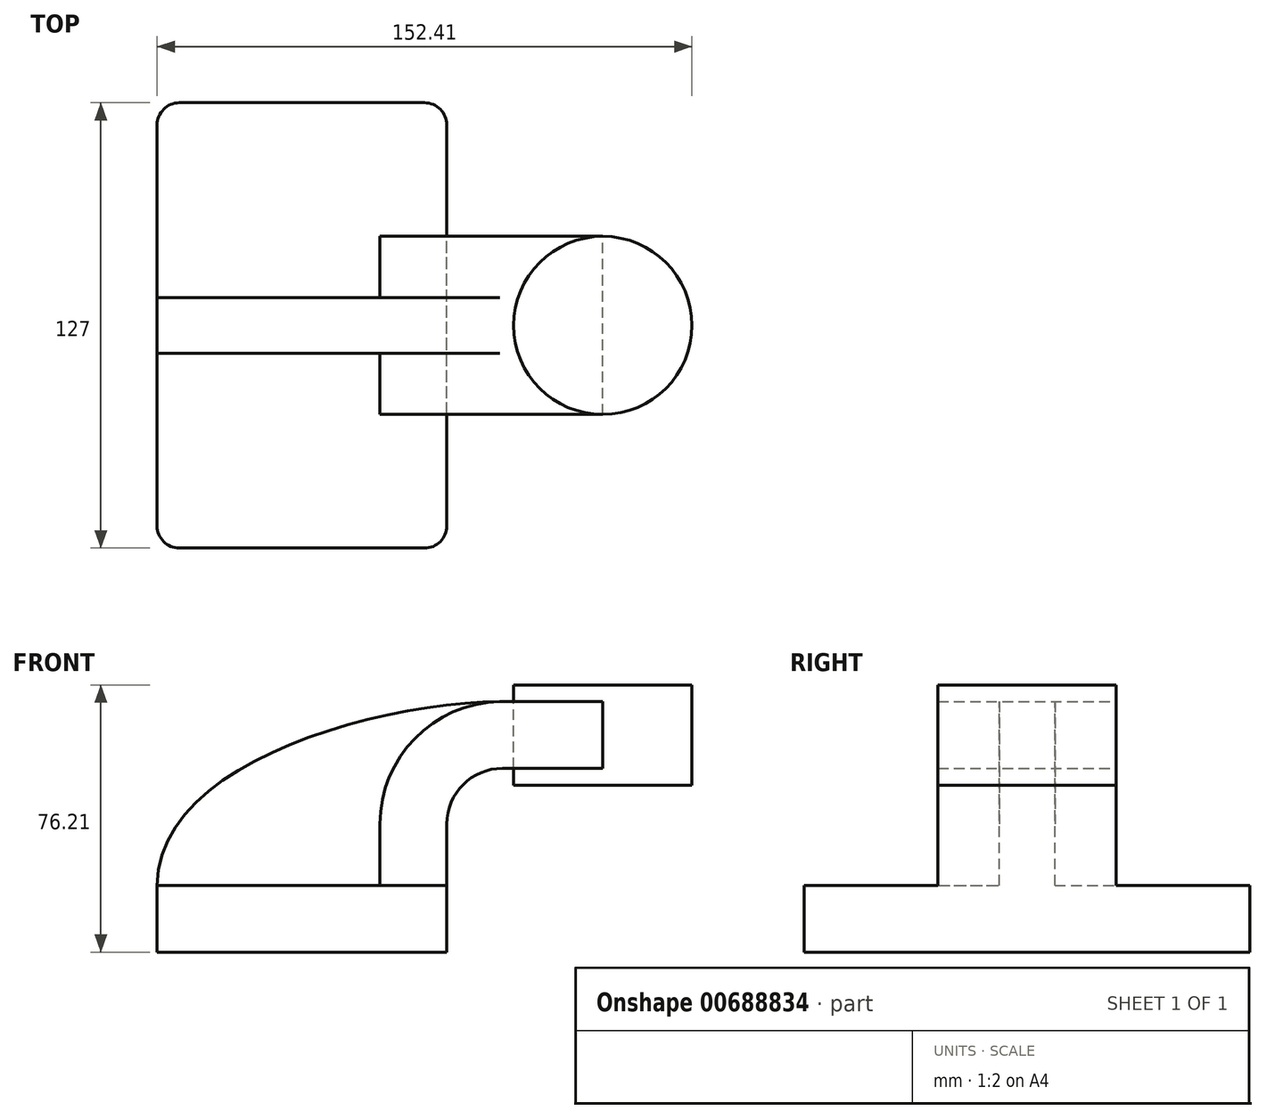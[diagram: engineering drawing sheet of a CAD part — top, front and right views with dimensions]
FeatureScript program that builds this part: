
annotation { "Feature Type Name" : "Feature", "Feature Type Description" : "" }
export const myFeature = defineFeature(function(context is Context, id is Id, definition is map)
    precondition{}
    {
        {
            var Q0;
            Q0=qCreatedBy(makeId("Front.planeOp"),FACE);
            var sketch = newSketch(context, id + "F0", { "sketchPlane" : qUnion([Q0])});
            skLineSegment(sketch, "E0.bottom", {"start": v(-41.28, 9.52) * mm, "end": v(41.27, 9.53) * mm});
            skLineSegment(sketch, "E0.top", {"start": v(-41.28, -9.53) * mm, "end": v(41.28, -9.53) * mm});
            skLineSegment(sketch, "E0.left", {"start": v(-41.28, 9.52) * mm, "end": v(-41.27, -9.53) * mm});
            skLineSegment(sketch, "E0.right", {"start": v(41.28, 9.53) * mm, "end": v(41.28, -9.52) * mm});
            skPoint(sketch, "E0.middle", {"position": v(0, 0) * mm});
            skLineSegment(sketch, "E1.bottom", {"start": v(60.32, 38.1) * mm, "end": v(111.12, 38.1) * mm});
            skLineSegment(sketch, "E1.top", {"start": v(60.32, 66.68) * mm, "end": v(111.12, 66.68) * mm});
            skLineSegment(sketch, "E1.left", {"start": v(60.32, 38.1) * mm, "end": v(60.32, 66.68) * mm});
            skLineSegment(sketch, "E1.right", {"start": v(111.12, 38.1) * mm, "end": v(111.12, 66.68) * mm});
            skPoint(sketch, "E1.middle", {"position": v(85.72, 52.39) * mm});
            skLineSegment(sketch, "E2", {"start": v(41.27, 9.53) * mm, "end": v(41.27, 27) * mm});
            skArc(sketch, "E3", {"start": v(41.27, 27) * mm, "mid": v(45.92, 38.23) * mm, "end": v(57.15, 42.88) * mm});
            skLineSegment(sketch, "E4", {"start": v(57.15, 42.88) * mm, "end": v(85.72, 42.88) * mm});
            skLineSegment(sketch, "E5.0", {"start": v(57.15, 61.93) * mm, "end": v(85.72, 61.93) * mm});
            skArc(sketch, "E5.1", {"start": v(22.22, 27) * mm, "mid": v(32.45, 51.7) * mm, "end": v(57.15, 61.93) * mm});
            skLineSegment(sketch, "E5.2", {"start": v(22.22, 9.53) * mm, "end": v(22.22, 27) * mm});
            skFitSpline(sketch, "E6", {"points": [v(-41.28, 9.53) * mm, v(57.15, 61.93) * mm], "startDerivative": vector(0.27, 104.66) * mm, "endDerivative": vector(108.7, 0.8) * mm});
            skLineSegment(sketch, "E7", {"start": v(85.72, 61.93) * mm, "end": v(85.72, 42.88) * mm});
            skLineSegment(sketch, "E8", {"start": v(60.32, 61.93) * mm, "end": v(60.32, 42.88) * mm});
            skLineSegment(sketch, "E9", {"start": v(85.72, 66.67) * mm, "end": v(85.72, 38.1) * mm});
            skSolve(sketch);
        }
        {
            var Q0;
            Q0=makeQuery(id+"F0.imprint","IMPRINT",FACE,{"disambiguationData":[TD([[makeQuery(id+"F0.imprint","IMPRINT",EDGE,{"derivedFrom":sQuery(id+"F0.wireOp",EDGE,"E0.top")}),1.0]])]});
            extrude(context, id + "F1", {"entities" : qUnion([Q0]), "endBound" : BoundingType.SYMMETRIC, "depth" : 127 * mm, "offsetDistance" : 25.4 * mm});
        }
        {
            var Q0;
            {var subQ0=sQuery(id+"F0.wireOp",EDGE,"E7");Q0=makeQuery(id+"F0.imprint","IMPRINT",FACE,{"disambiguationData":[TD([[makeQuery(id+"F0.imprint","IMPRINT",EDGE,{"derivedFrom":subQ0}),-1.0]])]});}
            var Q1;
            {var subQ4=sQuery(id+"F0.wireOp",EDGE,"E2");Q1=makeQuery(id+"F0.imprint","IMPRINT",FACE,{"disambiguationData":[TD([[makeQuery(id+"F0.imprint","IMPRINT",EDGE,{"derivedFrom":subQ4}),1.0]])]});}
            var Q2;
            {var subQ3=sQuery(id+"F0.wireOp",EDGE,"E8");Q2=makeQuery(id+"F0.imprint","IMPRINT",FACE,{"disambiguationData":[TD([[makeQuery(id+"F0.imprint","IMPRINT",EDGE,{"derivedFrom":subQ3}),1.0]])]});}
            extrude(context, id + "F2", {"entities" : qUnion([Q0, Q1, Q2]), "operationType" : NewBodyOperationType.ADD, "endBound" : BoundingType.SYMMETRIC, "depth" : 50.8 * mm, "offsetDistance" : 25.4 * mm});
        }
        {
            var Q0;
            {var subQ3=sQuery(id+"F0.wireOp",EDGE,"E5.2");Q0=makeQuery(id+"F0.imprint","IMPRINT",FACE,{"disambiguationData":[TD([[makeQuery(id+"F0.imprint","IMPRINT",EDGE,{"derivedFrom":subQ3}),1.0]])]});}
            extrude(context, id + "F3", {"entities" : qUnion([Q0]), "operationType" : NewBodyOperationType.ADD, "endBound" : BoundingType.SYMMETRIC, "depth" : 15.88 * mm, "offsetDistance" : 25.4 * mm});
        }
        {
            var Q0;
            {var subQ0=sQuery(id+"F0.wireOp",EDGE,"E1.right");Q0=makeQuery(id+"F0.imprint","IMPRINT",FACE,{"disambiguationData":[TD([[makeQuery(id+"F0.imprint","IMPRINT",EDGE,{"derivedFrom":subQ0}),1.0]])]});}
            var Q1;
            Q1=sQuery(id+"F0.wireOp",EDGE,"E9");
            revolve(context, id + "F4", {"entities" : qUnion([Q0]), "axis" : qUnion([Q1]), "revolveType" : RevolveType.FULL});
        }
        {
            var Q0;
            Q0=makeQuery(id+"F1.opExtrude","CAP_EDGE",EDGE,{"disambiguationData":[OSD([sQuery(id+"F0.wireOp",EDGE,"E0.left")])],"isStart":false});
            var Q1;
            Q1=makeQuery(id+"F1.opExtrude","CAP_EDGE",EDGE,{"disambiguationData":[OSD([sQuery(id+"F0.wireOp",EDGE,"E0.right")])],"isStart":false});
            var Q2;
            Q2=makeQuery(id+"F1.opExtrude","CAP_EDGE",EDGE,{"disambiguationData":[OSD([sQuery(id+"F0.wireOp",EDGE,"E0.left")])],"isStart":true});
            var Q3;
            Q3=makeQuery(id+"F1.opExtrude","CAP_EDGE",EDGE,{"disambiguationData":[OSD([sQuery(id+"F0.wireOp",EDGE,"E0.right")])],"isStart":true});
            fillet(context, id + "F5", {"entities" : qUnion([Q0, Q1, Q2, Q3]), "radius" : 6.35 * mm, "tangentPropagation" : true, "allowEdgeOverflow" : false});
        }
    });
